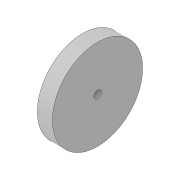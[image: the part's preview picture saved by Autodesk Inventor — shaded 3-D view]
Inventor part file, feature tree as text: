
AUTODESK INVENTOR PART (.ipt)
format: ipt  version: 2019.4 (Build 234330000, 330)  size: 82,432 bytes
history: native  units: in
note: dims shown in document units (in); Inventor stores cm internally (conversion verified against a paired STEP export)
features: revolve x1, sketch x1
ambient origin geometry x8: Origin, YZ Plane, XZ Plane, XY Plane, X Axis, Y Axis, Z Axis, Center Point
bodies: Solid1 (feature_tree)
feature tree (2):
  revolve  "Revolution1"  [1 undecoded]
  sketch  "Sketch2"  dims[d0=3.0in d1=1.0in d2=0.25in d3=90.0deg]
note: 1 required parameter value undecoded (feature->parameter linkage not recoverable at this tier; creation-order binding heuristic only, values carry confidence <= 0.55)
